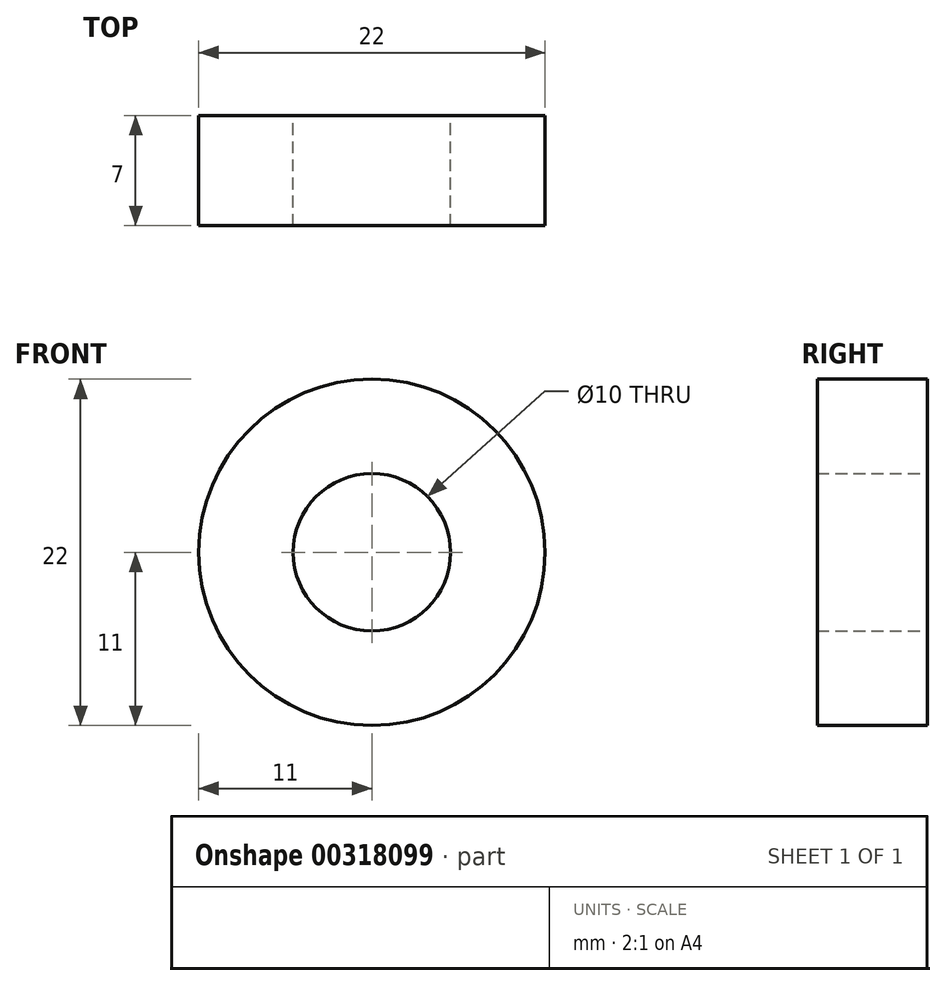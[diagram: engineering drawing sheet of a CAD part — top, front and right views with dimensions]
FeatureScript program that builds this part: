
annotation { "Feature Type Name" : "Feature", "Feature Type Description" : "" }
export const myFeature = defineFeature(function(context is Context, id is Id, definition is map)
    precondition{}
    {
        {
            var Q0;
            Q0=qCreatedBy(makeId("Front.planeOp"),FACE);
            var sketch = newSketch(context, id + "F0", { "sketchPlane" : qUnion([Q0])});
            skCircle(sketch, "E0", {"center": v(0, 0) * mm, "radius": 11 * mm});
            skCircle(sketch, "E1", {"center": v(0, 0) * mm, "radius": 5 * mm});
            skSolve(sketch);
        }
        {
            var Q0;
            Q0 = qSketchRegion(id + "F0", true);
            extrude(context, id + "F1", {"entities" : qUnion([Q0]), "depth" : 7 * mm});
        }
    });
